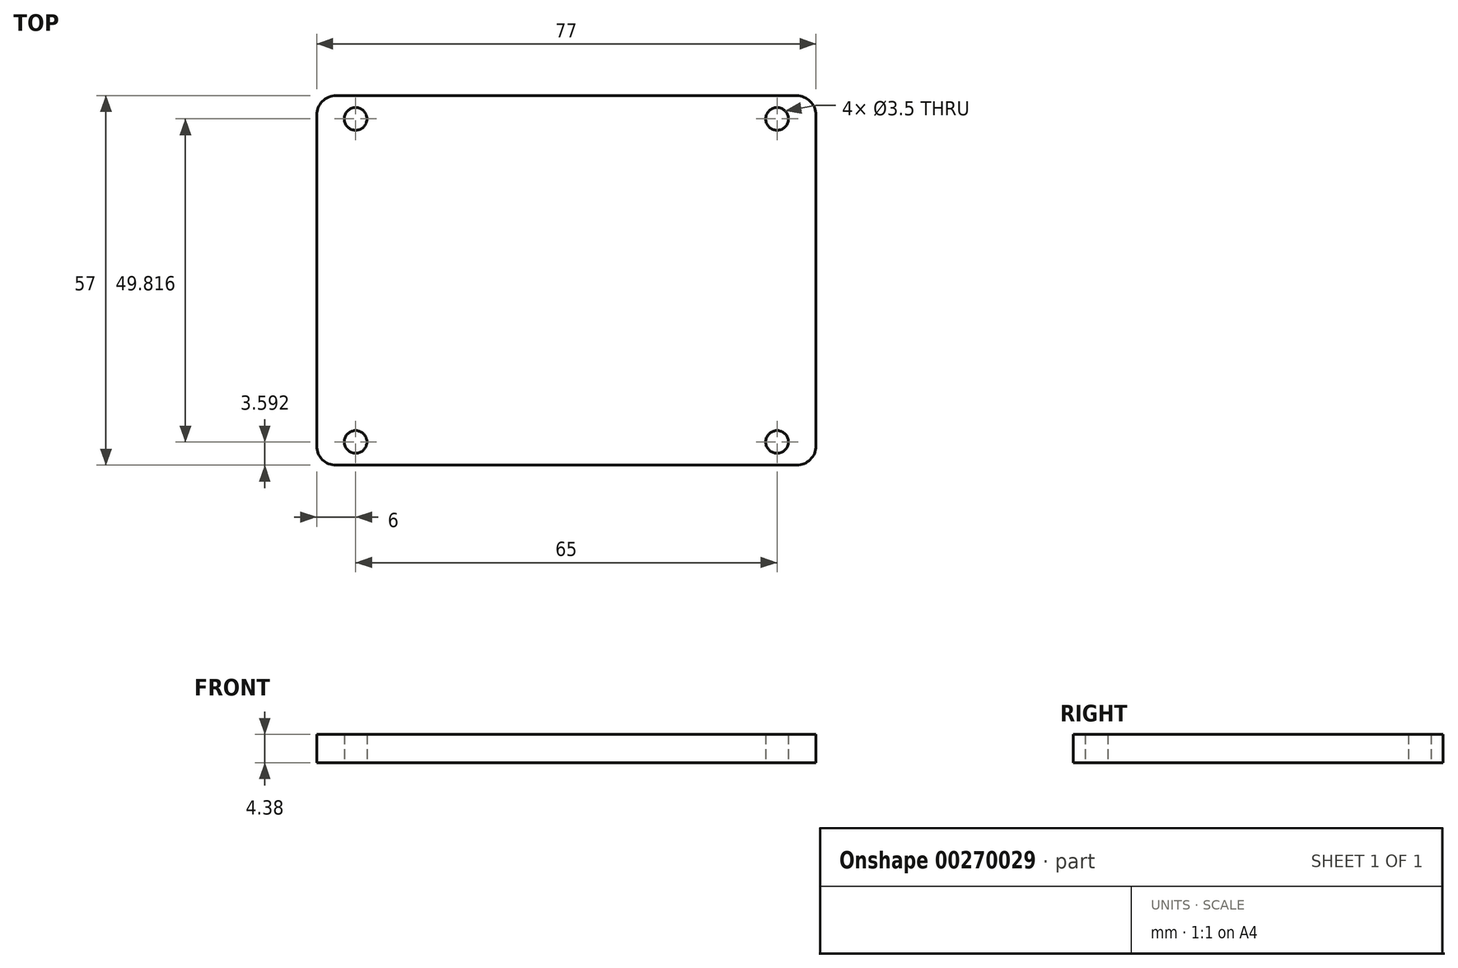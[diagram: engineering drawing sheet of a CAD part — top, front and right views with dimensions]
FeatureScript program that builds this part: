
annotation { "Feature Type Name" : "Feature", "Feature Type Description" : "" }
export const myFeature = defineFeature(function(context is Context, id is Id, definition is map)
    precondition{}
    {
        {
            var Q0;
            Q0=qCreatedBy(makeId("Top.planeOp"),FACE);
            var sketch = newSketch(context, id + "F0", { "sketchPlane" : qUnion([Q0])});
            skLineSegment(sketch, "E0.bottom", {"start": v(-38.5, -28.5) * mm, "end": v(38.5, -28.5) * mm});
            skLineSegment(sketch, "E0.top", {"start": v(-38.5, 28.5) * mm, "end": v(38.5, 28.5) * mm});
            skLineSegment(sketch, "E0.left", {"start": v(-38.5, -28.5) * mm, "end": v(-38.5, 28.5) * mm});
            skLineSegment(sketch, "E0.right", {"start": v(38.5, -28.5) * mm, "end": v(38.5, 28.5) * mm});
            skPoint(sketch, "E0.middle", {"position": v(0, 0) * mm});
            skCircle(sketch, "E1", {"center": v(-32.5, 24.9) * mm, "radius": 1.75 * mm});
            skCircle(sketch, "E2.MirrorC", {"center": v(32.5, 24.9) * mm, "radius": 1.75 * mm});
            skCircle(sketch, "E3.MirrorC", {"center": v(-32.5, -24.9) * mm, "radius": 1.75 * mm});
            skCircle(sketch, "E4.MirrorC", {"center": v(32.5, -24.9) * mm, "radius": 1.75 * mm});
            skSolve(sketch);
        }
        {
            var Q0;
            Q0 = qSketchRegion(id + "F0", true);
            extrude(context, id + "F1", {"entities" : qUnion([Q0]), "depth" : 4.38 * mm});
        }
        {
            var Q0;
            Q0 = qSketchRegion(id + "F0", true);
            extrude(context, id + "F2", {"entities" : qUnion([Q0]), "operationType" : NewBodyOperationType.ADD, "depth" : 3.2 * mm});
        }
        {
            var Q0;
            Q0=makeQuery(id+"F1.opExtrude","SWEPT_EDGE",EDGE,{"disambiguationData":[OSD([sQuery(id+"F0.wireOp",EDGE,"E0.top"),sQuery(id+"F0.wireOp",EDGE,"E0.left")])]});
            var Q1;
            Q1=makeQuery(id+"F1.opExtrude","SWEPT_EDGE",EDGE,{"disambiguationData":[OSD([sQuery(id+"F0.wireOp",EDGE,"E0.bottom"),sQuery(id+"F0.wireOp",EDGE,"E0.left")])]});
            var Q2;
            Q2=makeQuery(id+"F1.opExtrude","SWEPT_EDGE",EDGE,{"disambiguationData":[OSD([sQuery(id+"F0.wireOp",EDGE,"E0.bottom"),sQuery(id+"F0.wireOp",EDGE,"E0.right")])]});
            var Q3;
            Q3=makeQuery(id+"F1.opExtrude","SWEPT_EDGE",EDGE,{"disambiguationData":[OSD([sQuery(id+"F0.wireOp",EDGE,"E0.top"),sQuery(id+"F0.wireOp",EDGE,"E0.right")])]});
            fillet(context, id + "F3", {"entities" : qUnion([Q0, Q1, Q2, Q3]), "radius" : 3 * mm, "tangentPropagation" : true, "allowEdgeOverflow" : false});
        }
    });
